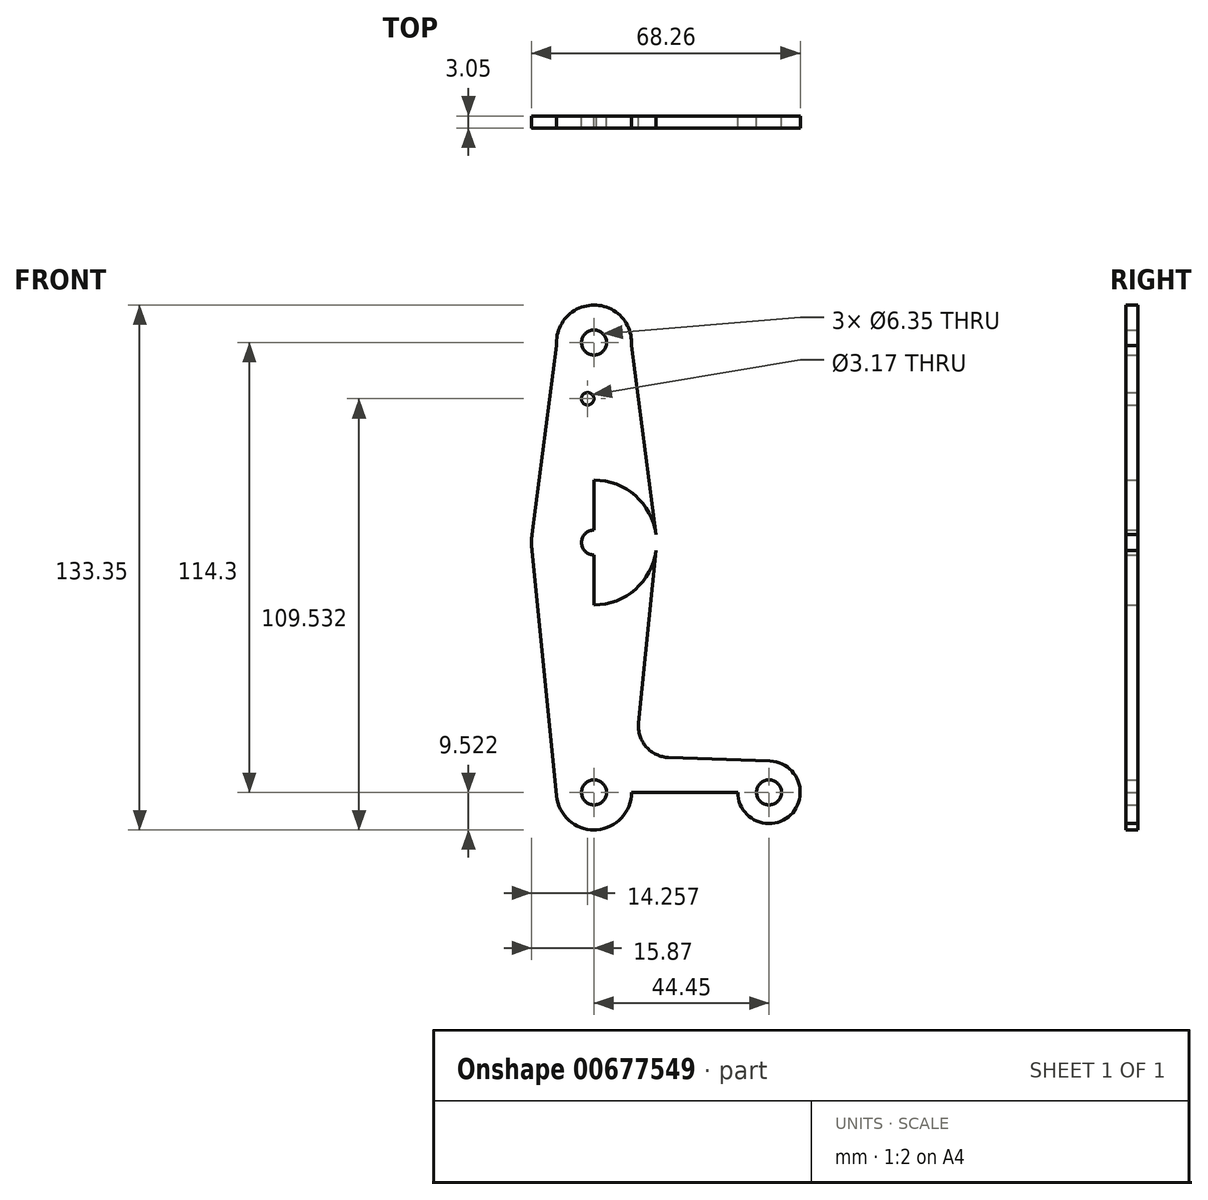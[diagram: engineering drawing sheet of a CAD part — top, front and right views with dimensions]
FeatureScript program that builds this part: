
annotation { "Feature Type Name" : "Feature", "Feature Type Description" : "" }
export const myFeature = defineFeature(function(context is Context, id is Id, definition is map)
    precondition{}
    {
        {
            var Q0;
            Q0=qCreatedBy(makeId("Front.planeOp"),FACE);
            var sketch = newSketch(context, id + "F0", { "sketchPlane" : qUnion([Q0])});
            skLineSegment(sketch, "E0", {"start": v(0, -66.4) * mm, "end": v(0, 47.9) * mm});
            skCircle(sketch, "E1", {"center": v(0, 47.9) * mm, "radius": 9.53 * mm});
            skCircle(sketch, "E2", {"center": v(0, -66.4) * mm, "radius": 9.53 * mm});
            skLineSegment(sketch, "E3", {"start": v(0, -66.4) * mm, "end": v(44.45, -66.4) * mm});
            skCircle(sketch, "E4", {"center": v(44.45, -66.4) * mm, "radius": 7.94 * mm});
            skCircle(sketch, "E5", {"center": v(0, -2.92) * mm, "radius": 15.88 * mm});
            skLineSegment(sketch, "E6", {"start": v(-9.5, 47.11) * mm, "end": v(-15.74, -0.87) * mm});
            skLineSegment(sketch, "E7", {"start": v(9.5, 47.15) * mm, "end": v(15.74, -0.88) * mm});
            skLineSegment(sketch, "E8", {"start": v(-15.74, -4.97) * mm, "end": v(-9.48, -67.36) * mm});
            skLineSegment(sketch, "E9", {"start": v(15.74, -4.97) * mm, "end": v(11.34, -48.82) * mm});
            skLineSegment(sketch, "E10", {"start": v(18.97, -57.56) * mm, "end": v(44.73, -58.48) * mm});
            skLineSegment(sketch, "E11", {"start": v(0, -75.93) * mm, "end": v(44.73, -74.34) * mm});
            skLineSegment(sketch, "E12", {"start": v(0, -2.92) * mm, "end": v(0, 33.6) * mm});
            skCircle(sketch, "E13", {"center": v(-1.61, 33.6) * mm, "radius": 1.59 * mm});
            skCircle(sketch, "E14", {"center": v(0, 47.9) * mm, "radius": 3.18 * mm});
            skCircle(sketch, "E15", {"center": v(0, -2.92) * mm, "radius": 3.18 * mm});
            skCircle(sketch, "E16", {"center": v(0, -66.4) * mm, "radius": 3.18 * mm});
            skCircle(sketch, "E17", {"center": v(44.45, -66.4) * mm, "radius": 3.18 * mm});
            skArc(sketch, "E18.filletArc", {"start": v(11.34, -48.82) * mm, "mid": v(13.26, -54.84) * mm, "end": v(18.97, -57.56) * mm});
            skSolve(sketch);
        }
        {
            var Q0;
            {var subQ0=sQuery(id+"F0.wireOp",EDGE,"E6");Q0=makeQuery(id+"F0.imprint","IMPRINT",FACE,{"disambiguationData":[TD([[makeQuery(id+"F0.imprint","IMPRINT",EDGE,{"derivedFrom":subQ0}),1.0]])]});}
            var Q1;
            {var subQ0=sQuery(id+"F0.wireOp",EDGE,"E7");Q1=makeQuery(id+"F0.imprint","IMPRINT",FACE,{"disambiguationData":[TD([[makeQuery(id+"F0.imprint","IMPRINT",EDGE,{"derivedFrom":subQ0}),-1.0]])]});}
            var Q2;
            Q2=makeQuery(id+"F0.imprint","IMPRINT",FACE,{"disambiguationData":[TD([[makeQuery(id+"F0.imprint","IMPRINT",EDGE,{"derivedFrom":sQuery(id+"F0.wireOp",EDGE,"E14")}),-1.0]])]});
            var Q3;
            {var subQ0=sQuery(id+"F0.wireOp",EDGE,"E5");var subQ5=sQuery(id+"F0.wireOp",EDGE,"E0");var subQ6=makeQuery(id+"F0.imprint","INTERSECT",VERTEX,{"derivedFrom":[subQ5,subQ0]});Q3=makeQuery(id+"F0.imprint","IMPRINT",FACE,{"disambiguationData":[TD([[makeQuery(id+"F0.imprint","IMPRINT",EDGE,{"disambiguationData":[TD([[subQ6,-1.0]])],"derivedFrom":subQ5}),1.0]])]});}
            var Q4;
            {var subQ0=sQuery(id+"F0.wireOp",EDGE,"E5");var subQ2=sQuery(id+"F0.wireOp",EDGE,"E0");var subQ3=makeQuery(id+"F0.imprint","INTERSECT",VERTEX,{"derivedFrom":[subQ2,subQ0]});Q4=makeQuery(id+"F0.imprint","IMPRINT",FACE,{"disambiguationData":[TD([[makeQuery(id+"F0.imprint","IMPRINT",EDGE,{"disambiguationData":[TD([[subQ3,-1.0]])],"derivedFrom":subQ2}),-1.0]])]});}
            var Q5;
            {var subQ10=sQuery(id+"F0.wireOp",EDGE,"E9");Q5=makeQuery(id+"F0.imprint","IMPRINT",FACE,{"disambiguationData":[TD([[makeQuery(id+"F0.imprint","IMPRINT",EDGE,{"derivedFrom":subQ10}),-1.0]])]});}
            var Q6;
            {var subQ0=sQuery(id+"F0.wireOp",EDGE,"E16");var subQ1=sQuery(id+"F0.wireOp",EDGE,"E0");var subQ2=makeQuery(id+"F0.imprint","INTERSECT",VERTEX,{"derivedFrom":[subQ1,subQ0]});Q6=makeQuery(id+"F0.imprint","IMPRINT",FACE,{"disambiguationData":[TD([[makeQuery(id+"F0.imprint","IMPRINT",EDGE,{"disambiguationData":[TD([[subQ2,-1.0]])],"derivedFrom":subQ1}),-1.0]])]});}
            var Q7;
            {var subQ6=sQuery(id+"F0.wireOp",EDGE,"E0");var subQ9=sQuery(id+"F0.wireOp",EDGE,"E16");var subQ10=makeQuery(id+"F0.imprint","INTERSECT",VERTEX,{"derivedFrom":[subQ6,subQ9]});Q7=makeQuery(id+"F0.imprint","IMPRINT",FACE,{"disambiguationData":[TD([[makeQuery(id+"F0.imprint","IMPRINT",EDGE,{"disambiguationData":[TD([[subQ10,-1.0]])],"derivedFrom":subQ6}),1.0]])]});}
            var Q8;
            {var subQ5=sQuery(id+"F0.wireOp",EDGE,"E8");Q8=makeQuery(id+"F0.imprint","IMPRINT",FACE,{"disambiguationData":[TD([[makeQuery(id+"F0.imprint","IMPRINT",EDGE,{"derivedFrom":subQ5}),1.0]])]});}
            var Q9;
            {var subQ0=sQuery(id+"F0.wireOp",EDGE,"E11");var subQ1=sQuery(id+"F0.wireOp",EDGE,"E2");var subQ2=makeQuery(id+"F0.imprint","INTERSECT",VERTEX,{"disambiguationData":[OD(1.0)],"derivedFrom":[subQ1,subQ0]});Q9=makeQuery(id+"F0.imprint","IMPRINT",FACE,{"disambiguationData":[TD([[makeQuery(id+"F0.imprint","IMPRINT",EDGE,{"disambiguationData":[TD([[subQ2,-1.0]])],"derivedFrom":subQ1}),-1.0]])]});}
            var Q10;
            Q10=makeQuery(id+"F0.imprint","IMPRINT",FACE,{"disambiguationData":[TD([[makeQuery(id+"F0.imprint","IMPRINT",EDGE,{"derivedFrom":sQuery(id+"F0.wireOp",EDGE,"E17")}),-1.0]])]});
            extrude(context, id + "F1", {"entities" : qUnion([Q0, Q1, Q2, Q3, Q4, Q5, Q6, Q7, Q8, Q9, Q10]), "depth" : 3.05 * mm, "offsetDistance" : 25.4 * mm});
        }
    });
